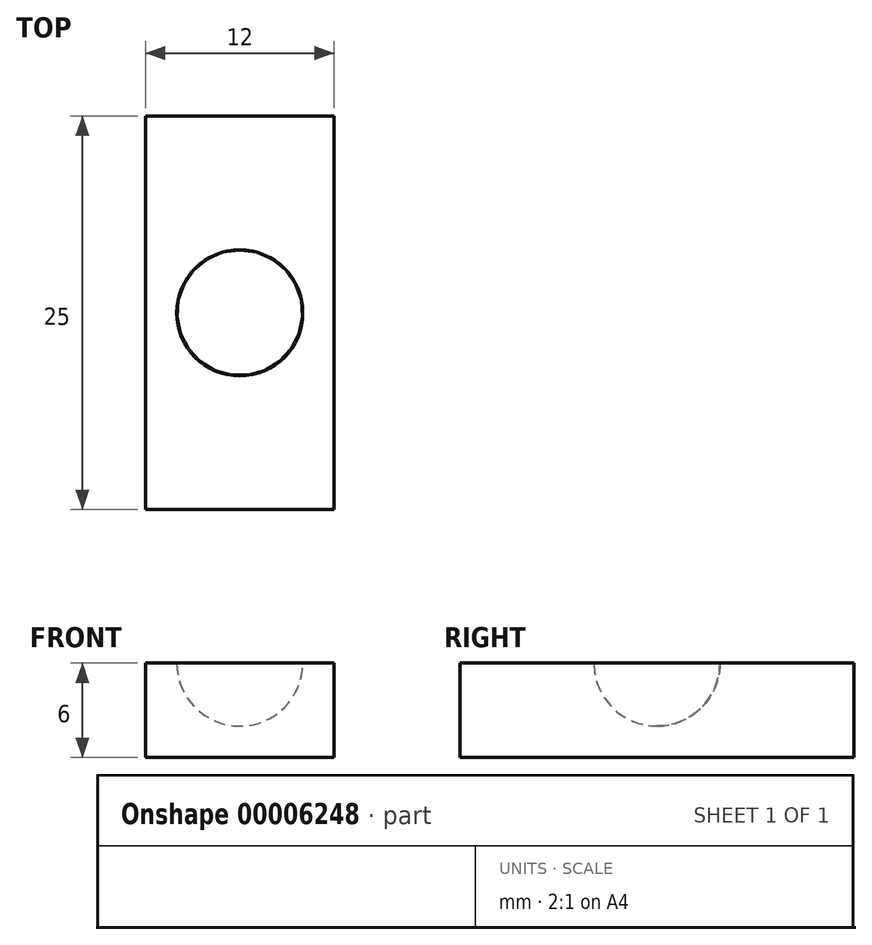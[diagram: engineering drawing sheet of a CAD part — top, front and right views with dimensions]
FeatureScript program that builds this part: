
annotation { "Feature Type Name" : "Feature", "Feature Type Description" : "" }
export const myFeature = defineFeature(function(context is Context, id is Id, definition is map)
    precondition{}
    {
        {
            var Q0;
            Q0=qCreatedBy(makeId("Front.planeOp"),FACE);
            var sketch = newSketch(context, id + "F0", { "sketchPlane" : qUnion([Q0])});
            skLineSegment(sketch, "E0.rect.bottom", {"start": v(-6, 3) * mm, "end": v(6, 3) * mm});
            skLineSegment(sketch, "E0.rect.top", {"start": v(-6, -3) * mm, "end": v(6, -3) * mm});
            skLineSegment(sketch, "E0.rect.left", {"start": v(-6, 3) * mm, "end": v(-6, -3) * mm});
            skLineSegment(sketch, "E0.rect.right", {"start": v(6, 3) * mm, "end": v(6, -3) * mm});
            skPoint(sketch, "E0.rect.middle", {"position": v(0, 0) * mm});
            skSolve(sketch);
        }
        {
            var Q0;
            Q0=makeQuery(id+"F0.imprint","IMPRINT",FACE,{"disambiguationData":[TD([[makeQuery(id+"F0.imprint","IMPRINT",EDGE,{"derivedFrom":sQuery(id+"F0.wireOp",EDGE,"E0.rect.bottom")}),-1.0]])]});
            extrude(context, id + "F1", {"entities" : qUnion([Q0]), "depth" : 25 * mm, "symmetric" : true});
        }
        {
            var Q0;
            Q0=qCreatedBy(makeId("Right.planeOp"),FACE);
            var sketch = newSketch(context, id + "F2", { "sketchPlane" : qUnion([Q0])});
            skPoint(sketch, "E1.start.orphan", {"position": v(0, -4.62) * mm});
            skArc(sketch, "E2", {"start": v(0, -1) * mm, "mid": v(2.83, 0.17) * mm, "end": v(4, 3) * mm});
            skLineSegment(sketch, "E3", {"start": v(0, 3) * mm, "end": v(0, -1) * mm});
            skLineSegment(sketch, "E4.bottom", {"start": v(0, 3) * mm, "end": v(4, 3) * mm});
            skLineSegment(sketch, "E4.top", {"start": v(0, 7) * mm, "end": v(4, 7) * mm});
            skLineSegment(sketch, "E4.left", {"start": v(0, 3) * mm, "end": v(0, 7) * mm});
            skLineSegment(sketch, "E4.right", {"start": v(4, 3) * mm, "end": v(4, 7) * mm});
            skSolve(sketch);
        }
        {
            var Q0;
            Q0=makeQuery(id+"F2.imprint","IMPRINT",FACE,{"disambiguationData":[TD([[makeQuery(id+"F2.imprint","IMPRINT",EDGE,{"derivedFrom":sQuery(id+"F2.wireOp",EDGE,"E4.bottom")}),1.0]])]});
            var Q1;
            Q1=makeQuery(id+"F2.imprint","IMPRINT",FACE,{"disambiguationData":[TD([[makeQuery(id+"F2.imprint","IMPRINT",EDGE,{"derivedFrom":sQuery(id+"F2.wireOp",EDGE,"E2")}),1.0]])]});
            var Q2;
            Q2=sQuery(id+"F2.wireOp",EDGE,"E3");
            revolve(context, id + "F3", {"operationType" : NewBodyOperationType.REMOVE, "entities" : qUnion([Q0, Q1]), "axis" : qUnion([Q2]), "revolveType" : RevolveType.FULL, "oppositeDirection" : true});
        }
    });
